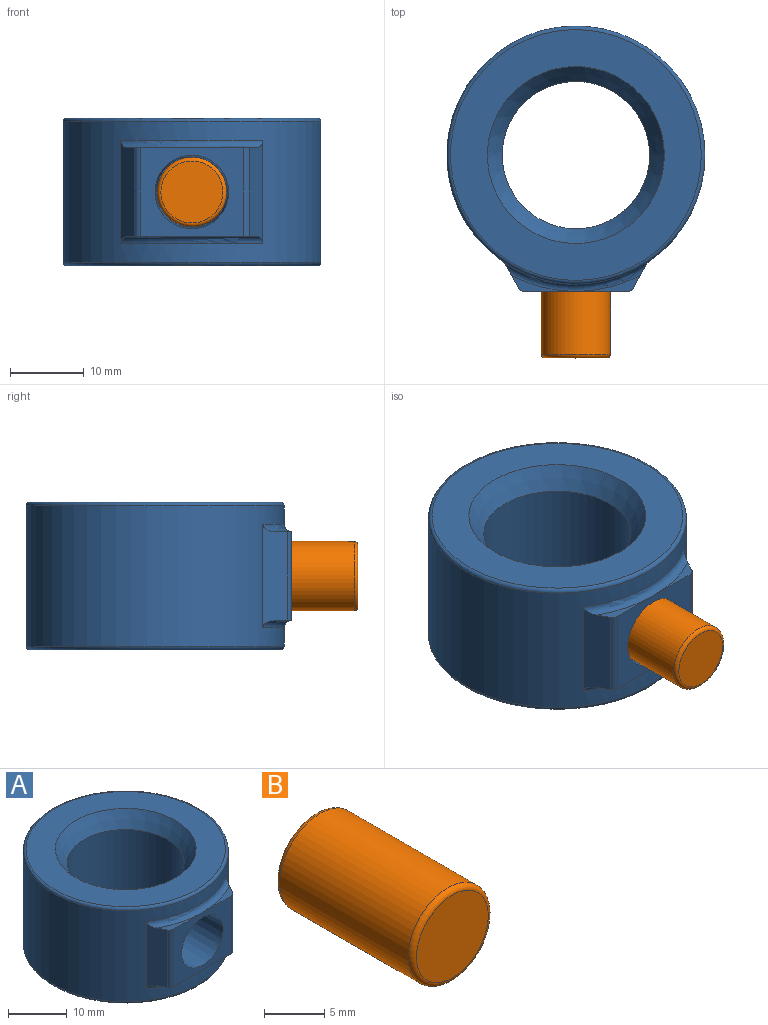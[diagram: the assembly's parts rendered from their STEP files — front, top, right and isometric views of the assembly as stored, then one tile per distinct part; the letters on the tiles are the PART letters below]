
ASSEMBLY  parts=2 mates=1
PART A: 21 faces, bbox 37.9x39.7x20 mm
  f0: plane 8.71x2.18mm, normal (0,0,1), area 4.8mm2, adj f2,f16,f18,f19
  f1: plane 8.71x2.18mm, normal (0,0,-1), area 4.8mm2, adj f2,f15,f17,f20
  f2: plane 13.88x12mm, normal (0,-1,0), area 88mm2, adj f0,f1,f9,f10,f13,f19,f20
  f3: plane 34x34mm, normal (0,0,1), area 455.5mm2, adj f8,f12
  f4: cylinder r=17.5mm len=35mm, axis (0,0,-1), area 1803.5mm2, adj f11,f12,f15,f16,f17,f18
  f5: cylinder r=10mm len=20mm, axis (0,0,-1), area 879.6mm2, adj f7,f8
  f6: plane 34x34mm, normal (0,0,-1), area 455.5mm2, adj f7,f11
  f7: cone r=12mm half-angle=33.7deg, axis (0,0,-1), area 249.2mm2, adj f5,f6
  f8: cone r=10mm half-angle=33.7deg, axis (0,0,1), area 249.2mm2, adj f3,f5
  f9: plane 8.71x2.18mm, normal (0,0,1), area 4.8mm2, adj f2,f15,f18,f20
  f10: plane 8.71x2.18mm, normal (0,0,-1), area 4.8mm2, adj f2,f16,f17,f19
  f11: torus R=17mm, axis (0,0,1), area 85.5mm2, adj f4,f6
  f12: torus R=17mm, axis (0,0,1), area 85.5mm2, adj f3,f4
  f13: cone r=5mm half-angle=1.5deg, axis (0,-1,0), area 216mm2, adj f2,f14
  f14: plane 9.63x9.63mm, normal (0,-1,0), area 72.9mm2, adj f13
  f15: plane 14x3.36mm, normal (-0.88,-0.47,0), area 46.7mm2, adj f1,f4,f9,f17,f18,f20
  f16: plane 14x3.36mm, normal (0.88,-0.47,0), area 46.7mm2, adj f0,f4,f10,f17,f18,f19
  f17: torus R=18.5mm, axis (0,0,-1), area 30.7mm2, adj f1,f4,f10,f15,f16
  f18: torus R=18.5mm, axis (0,0,1), area 30.7mm2, adj f0,f4,f9,f15,f16
  f19: cylinder r=1mm len=12mm, axis (0,0,-1), area 12.9mm2, adj f0,f2,f10,f16
  f20: cylinder r=1mm len=12mm, axis (0,0,1), area 12.9mm2, adj f1,f2,f9,f15
PART B: 5 faces, bbox 10.2x16x10.2 mm
  f0: cylinder r=4.7mm len=15mm, axis (0,1,0), area 443mm2, adj f3,f4
  f1: plane 8.4x8.4mm, normal (0,-1,0), area 55.4mm2, adj f4
  f2: plane 8.4x8.4mm, normal (0,1,0), area 55.4mm2, adj f3
  f3: torus R=4.2mm, axis (0,-1,0), area 22.3mm2, adj f0,f2
  f4: torus R=4.2mm, axis (0,-1,0), area 22.3mm2, adj f0,f1
PLACE A t=(0.01,-0.3,-10.01)mm
PLACE B t=(0.01,-11.8,-0.01)mm
MATE fastened B.f0 <-> A.f13  axis (0,1,0) through (0.01,-11.8,-0.01)mm
